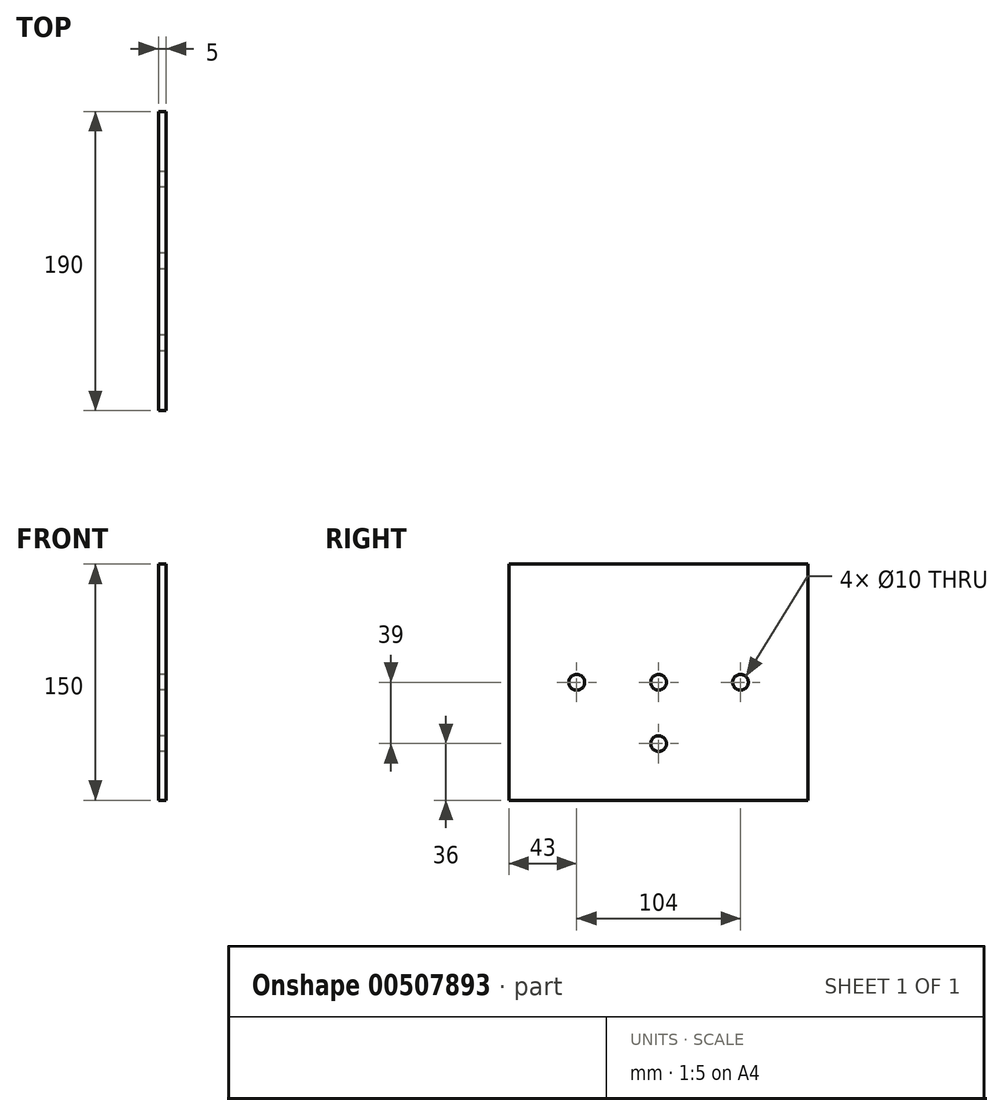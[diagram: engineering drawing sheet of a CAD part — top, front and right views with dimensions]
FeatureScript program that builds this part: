
annotation { "Feature Type Name" : "Feature", "Feature Type Description" : "" }
export const myFeature = defineFeature(function(context is Context, id is Id, definition is map)
    precondition{}
    {
        {
            var Q0;
            Q0=qCreatedBy(makeId("Right.planeOp"),FACE);
            var sketch = newSketch(context, id + "F0", { "sketchPlane" : qUnion([Q0])});
            skLineSegment(sketch, "E0.bottom", {"start": v(95, -75) * mm, "end": v(-95, -75) * mm});
            skLineSegment(sketch, "E0.top", {"start": v(95, 75) * mm, "end": v(-95, 75) * mm});
            skLineSegment(sketch, "E0.left", {"start": v(95, -75) * mm, "end": v(95, 75) * mm});
            skLineSegment(sketch, "E0.right", {"start": v(-95, -75) * mm, "end": v(-95, 75) * mm});
            skPoint(sketch, "E0.middle", {"position": v(0, 0) * mm});
            skLineSegment(sketch, "E1", {"start": v(-95, 75) * mm, "end": v(-95, 0) * mm});
            skLineSegment(sketch, "E2", {"start": v(-95, 0) * mm, "end": v(-45, 0) * mm});
            skLineSegment(sketch, "E3", {"start": v(-45, 0) * mm, "end": v(7, 0) * mm});
            skCircle(sketch, "E4", {"center": v(0, 0) * mm, "radius": 5 * mm});
            skLineSegment(sketch, "E5", {"start": v(0, 0) * mm, "end": v(52, 0) * mm});
            skCircle(sketch, "E6", {"center": v(52, 0) * mm, "radius": 5 * mm});
            skLineSegment(sketch, "E7", {"start": v(0, 0) * mm, "end": v(-52, 0) * mm});
            skCircle(sketch, "E8", {"center": v(-52, 0) * mm, "radius": 5 * mm});
            skLineSegment(sketch, "E9", {"start": v(0, 0) * mm, "end": v(0, -39) * mm});
            skCircle(sketch, "E10", {"center": v(0, -39) * mm, "radius": 5 * mm});
            skSolve(sketch);
        }
        {
            var Q0;
            Q0=makeQuery(id+"F0.imprint","IMPRINT",FACE,{"disambiguationData":[TD([[makeQuery(id+"F0.imprint","IMPRINT",EDGE,{"derivedFrom":sQuery(id+"F0.wireOp",EDGE,"E0.bottom")}),-1.0]])]});
            extrude(context, id + "F1", {"entities" : qUnion([Q0]), "depth" : 5 * mm, "offsetDistance" : 25 * mm});
        }
    });
